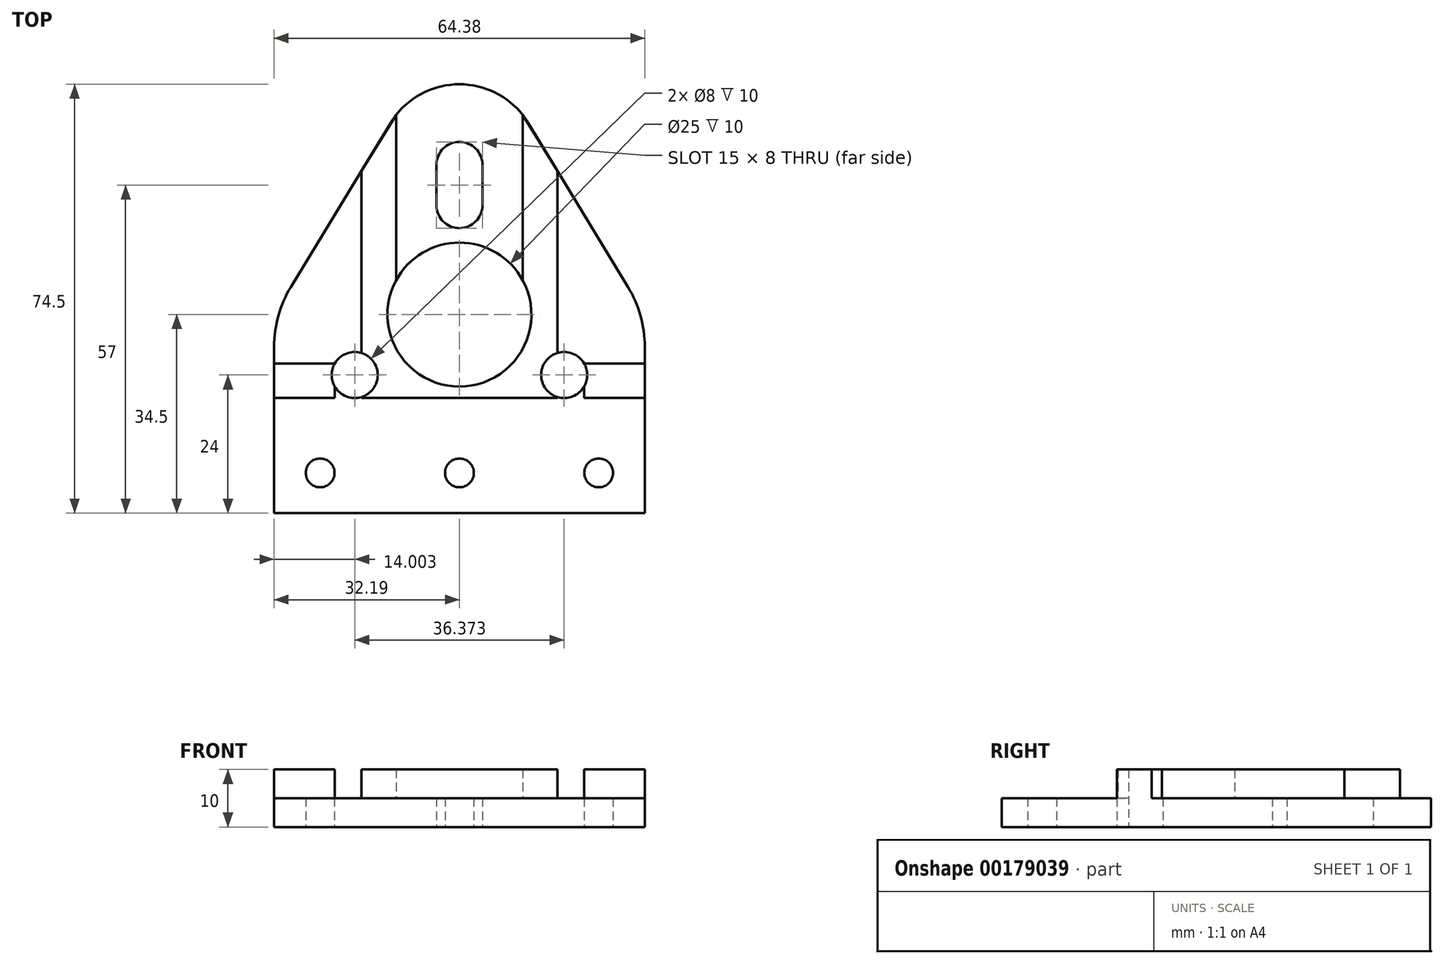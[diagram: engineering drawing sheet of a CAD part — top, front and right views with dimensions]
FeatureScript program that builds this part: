
annotation { "Feature Type Name" : "Feature", "Feature Type Description" : "" }
export const myFeature = defineFeature(function(context is Context, id is Id, definition is map)
    precondition{}
    {
        {
            var Q0;
            Q0=qCreatedBy(makeId("Top.planeOp"),FACE);
            var sketch = newSketch(context, id + "F0", { "sketchPlane" : qUnion([Q0])});
            skCircle(sketch, "E0", {"center": v(0, 0) * mm, "radius": 10 * mm, "construction": true});
            skCircle(sketch, "E1", {"center": v(0, 21) * mm, "radius": 11 * mm, "construction": true});
            skCircle(sketch, "E2.1.0", {"center": v(-18.19, -10.5) * mm, "radius": 11 * mm, "construction": true});
            skCircle(sketch, "E2.2.0", {"center": v(18.19, -10.5) * mm, "radius": 11 * mm, "construction": true});
            skCircle(sketch, "E3", {"center": v(-18.19, -10.5) * mm, "radius": 4 * mm});
            skCircle(sketch, "E4", {"center": v(18.19, -10.5) * mm, "radius": 4 * mm});
            skArc(sketch, "E5", {"start": v(-4, 21) * mm, "mid": v(0, 17) * mm, "end": v(4, 21) * mm, "construction": true});
            skArc(sketch, "E6", {"start": v(-4, 26) * mm, "mid": v(0, 30) * mm, "end": v(4, 26) * mm});
            skLineSegment(sketch, "E7", {"start": v(-4, 26) * mm, "end": v(-4, 21) * mm});
            skLineSegment(sketch, "E8", {"start": v(4, 26) * mm, "end": v(4, 21) * mm});
            skCircle(sketch, "E9", {"center": v(0, 0) * mm, "radius": 12.5 * mm});
            skLineSegment(sketch, "E10", {"start": v(-32.19, -34.5) * mm, "end": v(32.19, -34.5) * mm});
            skLineSegment(sketch, "E11", {"start": v(32.19, -34.5) * mm, "end": v(32.19, -5.6) * mm});
            skLineSegment(sketch, "E12.MirrorCS", {"start": v(-32.19, -34.5) * mm, "end": v(-32.19, -5.6) * mm});
            skArc(sketch, "E13", {"start": v(-11.96, 33.27) * mm, "mid": v(0, 40) * mm, "end": v(11.96, 33.27) * mm});
            skLineSegment(sketch, "E14", {"start": v(-29.28, 4.79) * mm, "end": v(-11.96, 33.27) * mm});
            skLineSegment(sketch, "E15", {"start": v(11.96, 33.27) * mm, "end": v(29.28, 4.79) * mm});
            skPoint(sketch, "E16.visualSharp", {"position": v(-32.19, 0) * mm});
            skArc(sketch, "E16.filletArc", {"start": v(-29.28, 4.79) * mm, "mid": v(-31.45, -0.2) * mm, "end": v(-32.19, -5.6) * mm});
            skPoint(sketch, "E17.visualSharp", {"position": v(32.19, 0) * mm});
            skArc(sketch, "E17.filletArc", {"start": v(32.19, -5.6) * mm, "mid": v(31.45, -0.2) * mm, "end": v(29.28, 4.79) * mm});
            skLineSegment(sketch, "E18", {"start": v(-4, 21) * mm, "end": v(-4, 19) * mm});
            skLineSegment(sketch, "E19.MirrorCS", {"start": v(4, 21) * mm, "end": v(4, 19) * mm});
            skArc(sketch, "E20", {"start": v(-4, 19) * mm, "mid": v(0, 15) * mm, "end": v(4, 19) * mm});
            skPoint(sketch, "E20.centerSnap0", {"position": v(0, 17) * mm});
            skCircle(sketch, "E21", {"center": v(0, -27.5) * mm, "radius": 2.5 * mm});
            skCircle(sketch, "E22", {"center": v(-24.19, -27.5) * mm, "radius": 2.5 * mm});
            skCircle(sketch, "E23.MirrorC", {"center": v(24.19, -27.5) * mm, "radius": 2.5 * mm});
            skSolve(sketch);
        }
        {
            var Q0;
            Q0 = qSketchRegion(id + "F0", true);
            extrude(context, id + "F1", {"entities" : qUnion([Q0]), "depth" : 5 * mm});
        }
        {
            var Q0;
            Q0=makeQuery(id+"F1.opExtrude","CAP_FACE",FACE,{"disambiguationData":[OSD([sQuery(id+"F0.wireOp",EDGE,"E3"),sQuery(id+"F0.wireOp",EDGE,"E4"),sQuery(id+"F0.wireOp",EDGE,"E6"),sQuery(id+"F0.wireOp",EDGE,"E7"),sQuery(id+"F0.wireOp",EDGE,"E8"),sQuery(id+"F0.wireOp",EDGE,"E9"),sQuery(id+"F0.wireOp",EDGE,"E10"),sQuery(id+"F0.wireOp",EDGE,"E11"),sQuery(id+"F0.wireOp",EDGE,"E12.MirrorCS"),sQuery(id+"F0.wireOp",EDGE,"E13"),sQuery(id+"F0.wireOp",EDGE,"E14"),sQuery(id+"F0.wireOp",EDGE,"E15"),sQuery(id+"F0.wireOp",EDGE,"E16.filletArc"),sQuery(id+"F0.wireOp",EDGE,"E17.filletArc"),sQuery(id+"F0.wireOp",EDGE,"E18"),sQuery(id+"F0.wireOp",EDGE,"E19.MirrorCS"),sQuery(id+"F0.wireOp",EDGE,"E20"),sQuery(id+"F0.wireOp",EDGE,"E21"),sQuery(id+"F0.wireOp",EDGE,"E22"),sQuery(id+"F0.wireOp",EDGE,"E23.MirrorC")])],"isStart":false});
            var sketch = newSketch(context, id + "F2", { "sketchPlane" : qUnion([Q0])});
            skLineSegment(sketch, "E24", {"start": v(-32.19, -14.5) * mm, "end": v(-21.65, -14.5) * mm});
            skLineSegment(sketch, "E25.0", {"start": v(-32.19, -34.5) * mm, "end": v(-32.19, -5.6) * mm});
            skLineSegment(sketch, "E26.0", {"start": v(32.19, -34.5) * mm, "end": v(32.19, -5.6) * mm});
            skLineSegment(sketch, "E27", {"start": v(-32.19, -8.5) * mm, "end": v(-21.65, -8.5) * mm});
            skArc(sketch, "E28.0", {"start": v(-21.65, -8.5) * mm, "mid": v(-22.19, -10.5) * mm, "end": v(-21.65, -12.5) * mm});
            skArc(sketch, "E29.0", {"start": v(14.72, -8.5) * mm, "mid": v(14.46, -11.96) * mm, "end": v(17, -14.32) * mm});
            skLineSegment(sketch, "E30.MirrorCS", {"start": v(32.19, -8.5) * mm, "end": v(21.65, -8.5) * mm});
            skLineSegment(sketch, "E31", {"start": v(-17, -6.68) * mm, "end": v(-17, 24.99) * mm});
            skLineSegment(sketch, "E32", {"start": v(-11, 5.94) * mm, "end": v(-11, 34.66) * mm});
            skLineSegment(sketch, "E33", {"start": v(-11, 34.66) * mm, "end": v(-17, 24.99) * mm});
            skArc(sketch, "E34.0", {"start": v(-11, 5.94) * mm, "mid": v(0, -12.5) * mm, "end": v(11, 5.94) * mm});
            skLineSegment(sketch, "E35.MirrorCS", {"start": v(11, 5.94) * mm, "end": v(11, 34.66) * mm});
            skLineSegment(sketch, "E36.MirrorCS", {"start": v(11, 34.66) * mm, "end": v(17, 24.99) * mm});
            skLineSegment(sketch, "E37.MirrorCS", {"start": v(17, -6.68) * mm, "end": v(17, 24.99) * mm});
            skPoint(sketch, "E38.end.orphan", {"position": v(-9.17, -8.5) * mm});
            skPoint(sketch, "E39.MirrorCS.end.orphan", {"position": v(9.17, -8.5) * mm});
            skLineSegment(sketch, "E40", {"start": v(-21.65, -12.5) * mm, "end": v(-21.65, -14.5) * mm});
            skLineSegment(sketch, "E41", {"start": v(-17, -14.32) * mm, "end": v(-17, -14.5) * mm});
            skLineSegment(sketch, "E42.MirrorCS", {"start": v(17, -14.32) * mm, "end": v(17, -14.5) * mm});
            skLineSegment(sketch, "E43.MirrorCS", {"start": v(21.65, -12.5) * mm, "end": v(21.65, -14.5) * mm});
            skLineSegment(sketch, "E44.trimOffspring", {"start": v(-17, -14.5) * mm, "end": v(17, -14.5) * mm});
            skArc(sketch, "E45.trimOffspring", {"start": v(-17, -14.32) * mm, "mid": v(-14.46, -11.96) * mm, "end": v(-14.72, -8.5) * mm});
            skLineSegment(sketch, "E46.trimOffspring", {"start": v(21.65, -14.5) * mm, "end": v(32.19, -14.5) * mm});
            skArc(sketch, "E47.trimOffspring", {"start": v(21.65, -12.5) * mm, "mid": v(22.19, -10.5) * mm, "end": v(21.65, -8.5) * mm});
            skArc(sketch, "E48.0", {"start": v(-17, -14.32) * mm, "mid": v(-14.19, -10.5) * mm, "end": v(-17, -6.68) * mm});
            skArc(sketch, "E49.0", {"start": v(17, -6.68) * mm, "mid": v(14.19, -10.5) * mm, "end": v(17, -14.32) * mm});
            skSolve(sketch);
        }
        {
            var Q0;
            Q0 = qSketchRegion(id + "F2", true);
            extrude(context, id + "F3", {"entities" : qUnion([Q0]), "operationType" : NewBodyOperationType.ADD, "depth" : 5 * mm});
        }
    });
